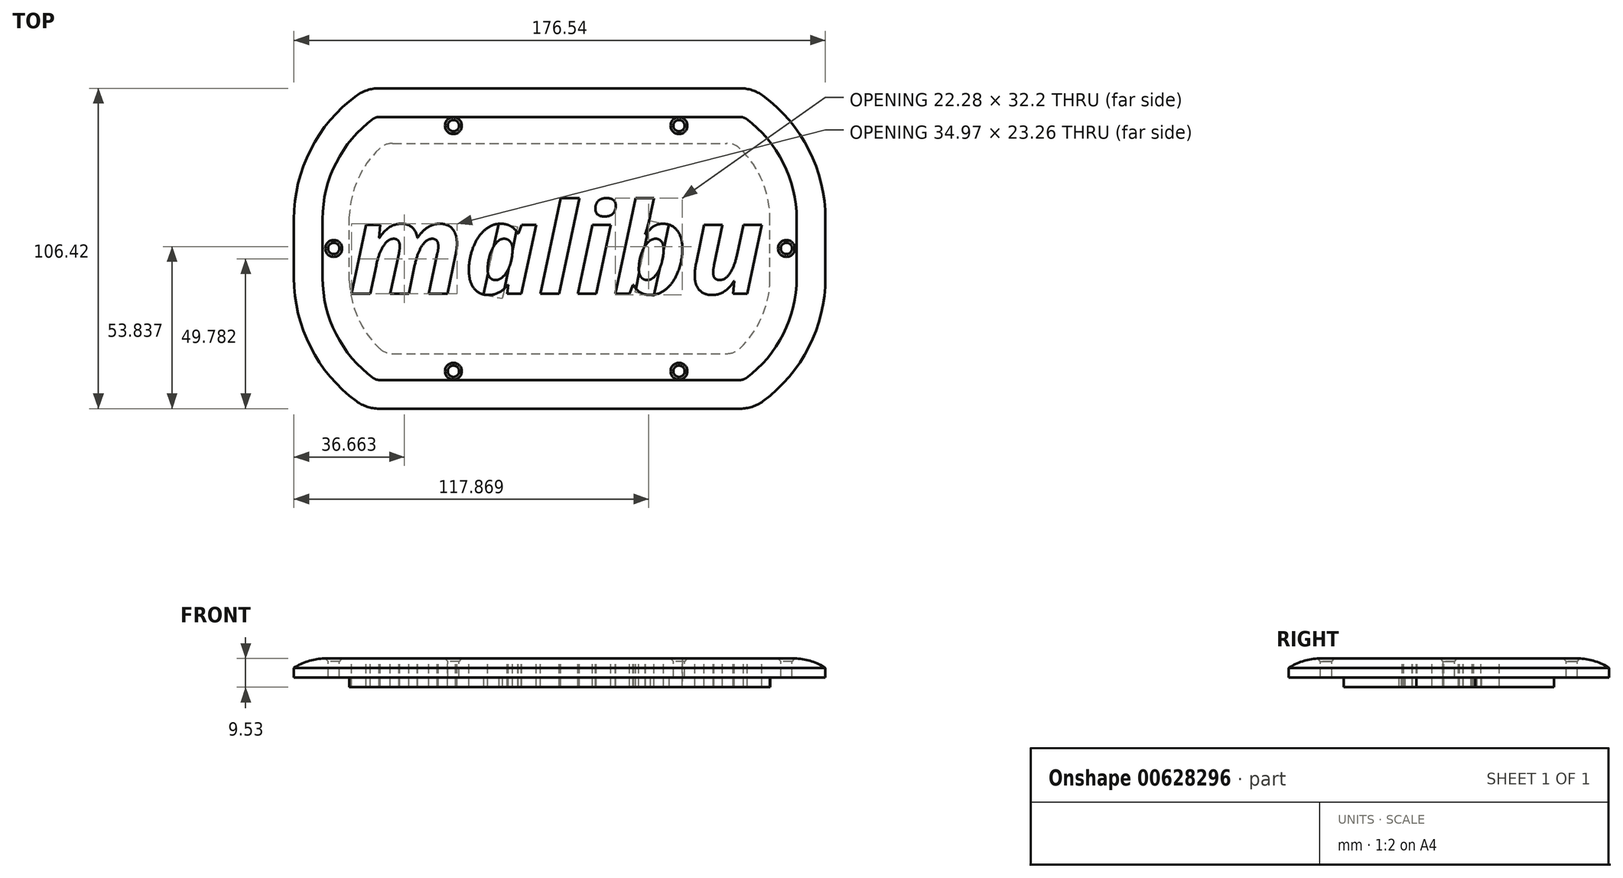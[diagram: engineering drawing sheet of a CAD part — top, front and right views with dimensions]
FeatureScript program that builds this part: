
annotation { "Feature Type Name" : "Feature", "Feature Type Description" : "" }
export const myFeature = defineFeature(function(context is Context, id is Id, definition is map)
    precondition{}
    {
        {
            var Q0;
            Q0=qCreatedBy(makeId("Top.planeOp"),FACE);
            var sketch = newSketch(context, id + "F0", { "sketchPlane" : qUnion([Q0])});
            skLineSegment(sketch, "E0.bottom", {"start": v(-63.81, 53.21) * mm, "end": v(63.81, 53.21) * mm});
            skLineSegment(sketch, "E0.top", {"start": v(-63.81, -53.21) * mm, "end": v(63.81, -53.21) * mm});
            skLineSegment(sketch, "E0.left", {"start": v(-88.27, 9.78) * mm, "end": v(-88.27, -9.78) * mm});
            skLineSegment(sketch, "E0.right", {"start": v(88.27, 9.78) * mm, "end": v(88.27, -9.78) * mm});
            skArc(sketch, "E1", {"start": v(-63.81, 53.21) * mm, "mid": v(-81.73, 34.7) * mm, "end": v(-88.27, 9.78) * mm});
            skArc(sketch, "E2", {"start": v(-88.27, -9.78) * mm, "mid": v(-81.73, -34.7) * mm, "end": v(-63.81, -53.21) * mm});
            skArc(sketch, "E3", {"start": v(63.81, -53.21) * mm, "mid": v(81.73, -34.7) * mm, "end": v(88.27, -9.78) * mm});
            skPoint(sketch, "E4", {"position": v(63.81, 53.21) * mm});
            skPoint(sketch, "E5", {"position": v(-68.68, 59.8) * mm});
            skPoint(sketch, "E6", {"position": v(-63.81, 53.21) * mm});
            skArc(sketch, "E7.trimOffspring", {"start": v(88.27, 9.78) * mm, "mid": v(81.73, 34.7) * mm, "end": v(63.81, 53.21) * mm});
            skSolve(sketch);
        }
        {
            var Q0;
            Q0 = qSketchRegion(id + "F0", true);
            extrude(context, id + "F1", {"entities" : qUnion([Q0]), "depth" : 9.52 * mm, "offsetDistance" : 25.4 * mm});
        }
        {
            var Q0;
            Q0=makeQuery(id+"F1.opExtrude","SWEPT_EDGE",EDGE,{"disambiguationData":[OSD([sQuery(id+"F0.wireOp",EDGE,"E0.bottom"),sQuery(id+"F0.wireOp",EDGE,"E7.trimOffspring")])]});
            var Q1;
            Q1=makeQuery(id+"F1.opExtrude","SWEPT_EDGE",EDGE,{"disambiguationData":[OSD([sQuery(id+"F0.wireOp",EDGE,"E0.bottom"),sQuery(id+"F0.wireOp",EDGE,"E1")])]});
            var Q2;
            Q2=makeQuery(id+"F1.opExtrude","SWEPT_EDGE",EDGE,{"disambiguationData":[OSD([sQuery(id+"F0.wireOp",EDGE,"E0.top"),sQuery(id+"F0.wireOp",EDGE,"E3")])]});
            var Q3;
            Q3=makeQuery(id+"F1.opExtrude","SWEPT_EDGE",EDGE,{"disambiguationData":[OSD([sQuery(id+"F0.wireOp",EDGE,"E0.top"),sQuery(id+"F0.wireOp",EDGE,"E2")])]});
            fillet(context, id + "F2", {"entities" : qUnion([Q0, Q1, Q2, Q3]), "radius" : 12.7 * mm, "tangentPropagation" : true, "allowEdgeOverflow" : false});
        }
        {
            var Q0;
            Q0=makeQuery(id+"F1.opExtrude","CAP_FACE",FACE,{"disambiguationData":[OSD([sQuery(id+"F0.wireOp",EDGE,"E0.bottom"),sQuery(id+"F0.wireOp",EDGE,"E0.top"),sQuery(id+"F0.wireOp",EDGE,"E0.left"),sQuery(id+"F0.wireOp",EDGE,"E0.right"),sQuery(id+"F0.wireOp",EDGE,"E1"),sQuery(id+"F0.wireOp",EDGE,"E2"),sQuery(id+"F0.wireOp",EDGE,"E3"),sQuery(id+"F0.wireOp",EDGE,"E7.trimOffspring")])],"isStart":false});
            var sketch = newSketch(context, id + "F3", { "sketchPlane" : qUnion([Q0])});
            skArc(sketch, "E8.0", {"start": v(-59.98, 43.69) * mm, "mid": v(-60.97, 43.53) * mm, "end": v(-61.86, 43.07) * mm});
            skArc(sketch, "E8.1", {"start": v(61.86, -43.07) * mm, "mid": v(74.28, -28.44) * mm, "end": v(78.74, -9.78) * mm});
            skLineSegment(sketch, "E8.2", {"start": v(78.74, 9.78) * mm, "end": v(78.74, -9.78) * mm});
            skArc(sketch, "E8.3", {"start": v(78.74, 9.78) * mm, "mid": v(74.28, 28.44) * mm, "end": v(61.86, 43.07) * mm});
            skArc(sketch, "E8.4", {"start": v(61.86, 43.07) * mm, "mid": v(60.97, 43.53) * mm, "end": v(59.98, 43.69) * mm});
            skArc(sketch, "E8.5", {"start": v(59.98, -43.69) * mm, "mid": v(60.97, -43.53) * mm, "end": v(61.86, -43.07) * mm});
            skLineSegment(sketch, "E8.6", {"start": v(-59.98, 43.69) * mm, "end": v(59.98, 43.69) * mm});
            skLineSegment(sketch, "E8.7", {"start": v(-59.98, -43.69) * mm, "end": v(59.98, -43.69) * mm});
            skArc(sketch, "E8.8", {"start": v(-61.86, -43.07) * mm, "mid": v(-60.97, -43.53) * mm, "end": v(-59.98, -43.69) * mm});
            skArc(sketch, "E8.9", {"start": v(-78.74, -9.78) * mm, "mid": v(-74.28, -28.44) * mm, "end": v(-61.86, -43.07) * mm});
            skLineSegment(sketch, "E8.10", {"start": v(-78.74, 9.78) * mm, "end": v(-78.74, -9.78) * mm});
            skArc(sketch, "E8.11", {"start": v(-61.86, 43.07) * mm, "mid": v(-74.28, 28.44) * mm, "end": v(-78.74, 9.78) * mm});
            skSolve(sketch);
        }
        {
            var Q0;
            Q0=qCreatedBy(makeId("Front.planeOp"),FACE);
            var sketch = newSketch(context, id + "F4", { "sketchPlane" : qUnion([Q0])});
            skArc(sketch, "E9", {"start": v(88.27, 6.35) * mm, "mid": v(83.72, 8.58) * mm, "end": v(78.74, 9.52) * mm});
            skLineSegment(sketch, "E10", {"start": v(88.27, 10.8) * mm, "end": v(88.27, 6.35) * mm});
            skLineSegment(sketch, "E11", {"start": v(78.74, 9.52) * mm, "end": v(78.74, 10.8) * mm});
            skLineSegment(sketch, "E12", {"start": v(78.74, 10.8) * mm, "end": v(88.27, 10.8) * mm});
            skSolve(sketch);
        }
        {
            var Q0;
            Q0 = qSketchRegion(id + "F4", true);
            var Q1;
            Q1 = qConstructionFilter(qBodyType(qCreatedBy(id + "F3" ,EDGE), BodyType.WIRE), ConstructionObject.NO);
            sweep(context, id + "F5", {"operationType" : NewBodyOperationType.REMOVE, "profiles" : qUnion([Q0]), "path" : qUnion([Q1])});
        }
        {
            var Q0;
            Q0=makeQuery(id+"F1.opExtrude","CAP_FACE",FACE,{"disambiguationData":[OSD([sQuery(id+"F0.wireOp",EDGE,"E0.bottom"),sQuery(id+"F0.wireOp",EDGE,"E0.top"),sQuery(id+"F0.wireOp",EDGE,"E0.left"),sQuery(id+"F0.wireOp",EDGE,"E0.right"),sQuery(id+"F0.wireOp",EDGE,"E1"),sQuery(id+"F0.wireOp",EDGE,"E2"),sQuery(id+"F0.wireOp",EDGE,"E3"),sQuery(id+"F0.wireOp",EDGE,"E7.trimOffspring")])],"isStart":true});
            var sketch = newSketch(context, id + "F6", { "sketchPlane" : qUnion([Q0])});
            skLineSegment(sketch, "E13.bottom", {"start": v(-55.5, 34.93) * mm, "end": v(55.5, 34.93) * mm});
            skLineSegment(sketch, "E13.top", {"start": v(-55.5, -34.93) * mm, "end": v(55.5, -34.93) * mm});
            skLineSegment(sketch, "E13.right", {"start": v(69.85, 10.75) * mm, "end": v(69.85, -8.8) * mm});
            skArc(sketch, "E14", {"start": v(-59.9, 33.16) * mm, "mid": v(-67.08, 22.93) * mm, "end": v(-69.85, 10.75) * mm});
            skArc(sketch, "E15", {"start": v(-69.85, -10.75) * mm, "mid": v(-67.08, -22.93) * mm, "end": v(-59.9, -33.16) * mm});
            skArc(sketch, "E16", {"start": v(59.9, -33.16) * mm, "mid": v(67.46, -22.04) * mm, "end": v(69.85, -8.8) * mm});
            skArc(sketch, "E17", {"start": v(59.9, 33.16) * mm, "mid": v(67.08, 22.93) * mm, "end": v(69.85, 10.75) * mm});
            skLineSegment(sketch, "E18", {"start": v(-69.85, 10.75) * mm, "end": v(-69.85, -10.75) * mm});
            skPoint(sketch, "E19.visualSharp", {"position": v(-57.9, -34.93) * mm});
            skArc(sketch, "E19.filletArc", {"start": v(-59.9, -33.16) * mm, "mid": v(-57.87, -34.47) * mm, "end": v(-55.5, -34.93) * mm});
            skPoint(sketch, "E20.visualSharp", {"position": v(57.9, -34.93) * mm});
            skArc(sketch, "E20.filletArc", {"start": v(55.5, -34.93) * mm, "mid": v(57.87, -34.47) * mm, "end": v(59.9, -33.16) * mm});
            skPoint(sketch, "E21.visualSharp", {"position": v(57.9, 34.93) * mm});
            skArc(sketch, "E21.filletArc", {"start": v(59.9, 33.16) * mm, "mid": v(57.87, 34.47) * mm, "end": v(55.5, 34.93) * mm});
            skPoint(sketch, "E22.visualSharp", {"position": v(-57.9, 34.93) * mm});
            skArc(sketch, "E22.filletArc", {"start": v(-55.5, 34.92) * mm, "mid": v(-57.87, 34.47) * mm, "end": v(-59.9, 33.16) * mm});
            skSolve(sketch);
        }
        {
            var Q0;
            Q0=makeQuery(id+"F6.imprint","IMPRINT",FACE,{"disambiguationData":[TD([[makeQuery(id+"F6.imprint","IMPRINT",EDGE,{"derivedFrom":sQuery(id+"F6.wireOp",EDGE,"E13.bottom")}),1.0]])]});
            extrude(context, id + "F7", {"entities" : qUnion([Q0]), "operationType" : NewBodyOperationType.REMOVE, "oppositeDirection" : true, "depth" : 3.17 * mm, "offsetDistance" : 25.4 * mm});
        }
        {
            var Q0;
            Q0=makeQuery(id+"F1.opExtrude","CAP_FACE",FACE,{"disambiguationData":[OSD([sQuery(id+"F0.wireOp",EDGE,"E0.bottom"),sQuery(id+"F0.wireOp",EDGE,"E0.top"),sQuery(id+"F0.wireOp",EDGE,"E0.left"),sQuery(id+"F0.wireOp",EDGE,"E0.right"),sQuery(id+"F0.wireOp",EDGE,"E1"),sQuery(id+"F0.wireOp",EDGE,"E2"),sQuery(id+"F0.wireOp",EDGE,"E3"),sQuery(id+"F0.wireOp",EDGE,"E7.trimOffspring")])],"isStart":false});
            var sketch = newSketch(context, id + "F8", { "sketchPlane" : qUnion([Q0])});
            skPoint(sketch, "E23", {"position": v(-75.06, 0) * mm});
            skPoint(sketch, "E24", {"position": v(75.31, 0) * mm});
            skPoint(sketch, "E25", {"position": v(39.63, 40.8) * mm});
            skPoint(sketch, "E26", {"position": v(-35.3, 40.8) * mm});
            skPoint(sketch, "E27", {"position": v(-35.3, -40.8) * mm});
            skPoint(sketch, "E28", {"position": v(39.63, -40.8) * mm});
            skSolve(sketch);
        }
        {
            var Q0;
            Q0=sQuery(id+"F8.wireOp",VERTEX,"E23");
            var Q1;
            Q1=sQuery(id+"F8.wireOp",VERTEX,"E26");
            var Q2;
            Q2=sQuery(id+"F8.wireOp",VERTEX,"E25");
            var Q3;
            Q3=sQuery(id+"F8.wireOp",VERTEX,"E24");
            var Q4;
            Q4=sQuery(id+"F8.wireOp",VERTEX,"E28");
            var Q5;
            Q5=sQuery(id+"F8.wireOp",VERTEX,"E27");
            var Q6;
            Q6=makeQuery(id+"F1.opExtrude","SWEPT_BODY",BODY,{"disambiguationData":[OSD([sQuery(id+"F0.wireOp",EDGE,"E0.bottom"),sQuery(id+"F0.wireOp",EDGE,"E0.top"),sQuery(id+"F0.wireOp",EDGE,"E0.left"),sQuery(id+"F0.wireOp",EDGE,"E0.right"),sQuery(id+"F0.wireOp",EDGE,"E1"),sQuery(id+"F0.wireOp",EDGE,"E2"),sQuery(id+"F0.wireOp",EDGE,"E3"),sQuery(id+"F0.wireOp",EDGE,"E7.trimOffspring")])]});
            hole(context, id + "F9", {"style" : HoleStyle.C_SINK, "endStyle" : HoleEndStyle.THROUGH, "holeDiameter" : 3.76 * mm, "cSinkDiameter" : 5.6 * mm, "cSinkAngle" : 82 * degree, "majorDiameter" : 6.35 * mm, "isTappedThrough" : true, "tappedDepth" : 12.7 * mm, "tapClearance" : 3, "locations" : qUnion([Q0, Q1, Q2, Q3, Q4, Q5]), "scope" : qUnion([Q6])});
        }
        {
            var Q0;
            Q0=makeQuery(id+"F1.opExtrude","CAP_FACE",FACE,{"disambiguationData":[OSD([sQuery(id+"F0.wireOp",EDGE,"E0.bottom"),sQuery(id+"F0.wireOp",EDGE,"E0.top"),sQuery(id+"F0.wireOp",EDGE,"E0.left"),sQuery(id+"F0.wireOp",EDGE,"E0.right"),sQuery(id+"F0.wireOp",EDGE,"E1"),sQuery(id+"F0.wireOp",EDGE,"E2"),sQuery(id+"F0.wireOp",EDGE,"E3"),sQuery(id+"F0.wireOp",EDGE,"E7.trimOffspring")])],"isStart":false});
            var sketch = newSketch(context, id + "F10", { "sketchPlane" : qUnion([Q0])});
            skText(sketch, "E29", { "text": "malibu", "fontName": "OpenSans-BoldItalic.ttf"});
            const initialGuessF10  = {"E29": [-0.06985, -0.01506, 1, 0, 0.03012]};
            skSetInitialGuess(sketch, initialGuessF10);
            skSolve(sketch);
        }
        {
            var Q0;
            Q0 = qSketchRegion(id + "F10", true);
            extrude(context, id + "F11", {"entities" : qUnion([Q0]), "operationType" : NewBodyOperationType.REMOVE, "oppositeDirection" : true, "depth" : 25.4 * mm, "offsetDistance" : 25.4 * mm});
        }
        {
            var Q0;
            Q0=makeQuery(id+"F11.boolean.opBoolean","SPLIT",FACE,{"disambiguationData":[TD([makeQuery(id+"F7.boolean.opBoolean","COPY",FACE,{"derivedFrom":makeQuery(id+"F7.opExtrude","SWEPT_FACE",FACE,{"disambiguationData":[OSD([sQuery(id+"F6.wireOp",EDGE,"E13.bottom")])]})})])],"derivedFrom":makeQuery(id+"F1.opExtrude","CAP_FACE",FACE,{"disambiguationData":[OSD([sQuery(id+"F0.wireOp",EDGE,"E0.bottom"),sQuery(id+"F0.wireOp",EDGE,"E0.top"),sQuery(id+"F0.wireOp",EDGE,"E0.left"),sQuery(id+"F0.wireOp",EDGE,"E0.right"),sQuery(id+"F0.wireOp",EDGE,"E1"),sQuery(id+"F0.wireOp",EDGE,"E2"),sQuery(id+"F0.wireOp",EDGE,"E3"),sQuery(id+"F0.wireOp",EDGE,"E7.trimOffspring")])],"isStart":true})});
            var sketch = newSketch(context, id + "F12", { "sketchPlane" : qUnion([Q0])});
            skLineSegment(sketch, "E30", {"start": v(-25.29, 15.3) * mm, "end": v(-20.22, -8.52) * mm});
            skLineSegment(sketch, "E31", {"start": v(-20.22, -8.52) * mm, "end": v(-14, -7.2) * mm});
            skLineSegment(sketch, "E32", {"start": v(-14, -7.2) * mm, "end": v(-19.08, 16.62) * mm});
            skLineSegment(sketch, "E33", {"start": v(25.04, 14.57) * mm, "end": v(30.09, -9.26) * mm});
            skLineSegment(sketch, "E34", {"start": v(30.09, -9.26) * mm, "end": v(36.3, -7.94) * mm});
            skLineSegment(sketch, "E35", {"start": v(36.3, -7.94) * mm, "end": v(31.25, 15.88) * mm});
            skLineSegment(sketch, "E36", {"start": v(31.25, 15.88) * mm, "end": v(25.04, 14.57) * mm});
            skPoint(sketch, "E37", {"position": v(30.34, 4.84) * mm});
            skLineSegment(sketch, "E38", {"start": v(32.93, 7.26) * mm, "end": v(27.1, 1.79) * mm, "construction": true});
            skLineSegment(sketch, "E39", {"start": v(34.3, 2.82) * mm, "end": v(26.27, 6.9) * mm, "construction": true});
            skLineSegment(sketch, "E40", {"start": v(-25.29, 15.3) * mm, "end": v(-19.08, 16.62) * mm});
            skPoint(sketch, "E41.orphan", {"position": v(-15.54, 0) * mm});
            skPoint(sketch, "E42", {"position": v(-19.82, 4.84) * mm});
            skLineSegment(sketch, "E43", {"start": v(-22.38, 10.3) * mm, "end": v(-16.47, -2.27) * mm, "construction": true});
            skSolve(sketch);
        }
        {
            var Q0;
            Q0 = qSketchRegion(id + "F12", true);
            extrude(context, id + "F13", {"entities" : qUnion([Q0]), "oppositeDirection" : true, "depth" : 3.17 * mm, "offsetDistance" : 25.4 * mm});
        }
    });
